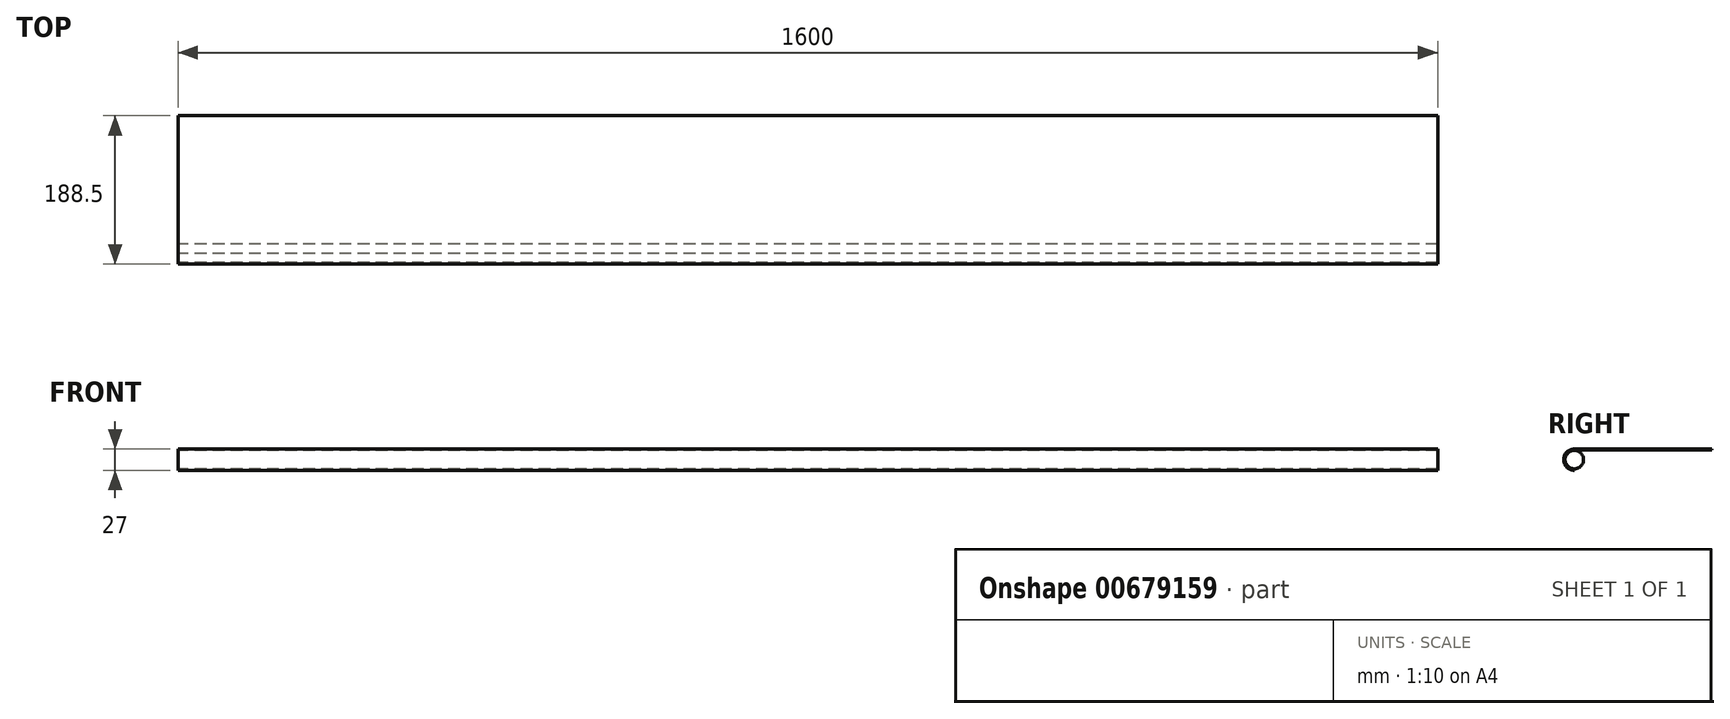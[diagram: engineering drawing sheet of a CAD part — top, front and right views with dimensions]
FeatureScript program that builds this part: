
annotation { "Feature Type Name" : "Feature", "Feature Type Description" : "" }
export const myFeature = defineFeature(function(context is Context, id is Id, definition is map)
    precondition{}
    {
        {
            var Q0;
            Q0=qCreatedBy(makeId("Right.planeOp"),FACE);
            var sketch = newSketch(context, id + "F0", { "sketchPlane" : qUnion([Q0])});
            skArc(sketch, "E0", {"start": v(-175, 13.5) * mm, "mid": v(-188.5, 0) * mm, "end": v(-175, -13.5) * mm});
            skArc(sketch, "E1.MirrorC", {"start": v(-175, -13.5) * mm, "mid": v(-188.5, 0) * mm, "end": v(-175, 13.5) * mm});
            skLineSegment(sketch, "E2", {"start": v(-175, 13.5) * mm, "end": v(0, 13.5) * mm});
            skPoint(sketch, "E3.start.orphan", {"position": v(-175, -13.5) * mm});
            skLineSegment(sketch, "E4.0", {"start": v(-175, 12) * mm, "end": v(0, 12) * mm});
            skArc(sketch, "E4.1", {"start": v(-175, -12) * mm, "mid": v(-187, 0) * mm, "end": v(-175, 12) * mm});
            skLineSegment(sketch, "E5", {"start": v(-175, -12) * mm, "end": v(-175, -13.5) * mm});
            skLineSegment(sketch, "E6", {"start": v(0, 13.5) * mm, "end": v(0, 12) * mm});
            skCircle(sketch, "E7", {"center": v(-175, 0) * mm, "radius": 11.75 * mm});
            skSolve(sketch);
        }
        {
            var Q0;
            Q0 = qSketchRegion(id + "F0", true);
            extrude(context, id + "F1", {"entities" : qUnion([Q0]), "endBound" : BoundingType.SYMMETRIC, "depth" : 1600 * mm, "offsetDistance" : 25 * mm});
        }
    });
